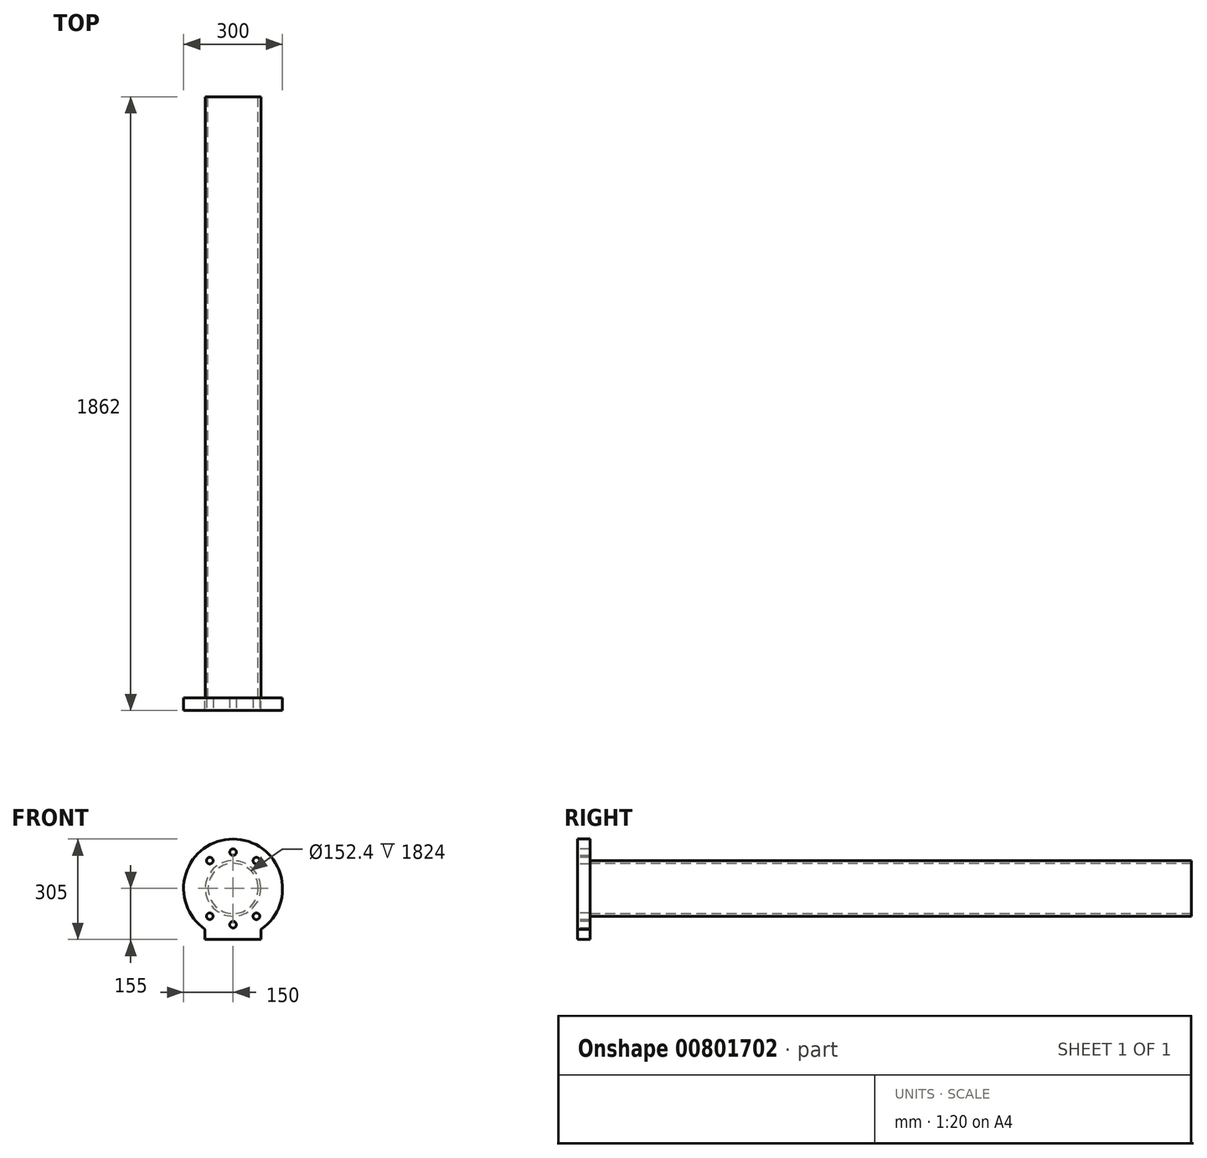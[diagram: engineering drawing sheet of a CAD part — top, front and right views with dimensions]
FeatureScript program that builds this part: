
annotation { "Feature Type Name" : "Feature", "Feature Type Description" : "" }
export const myFeature = defineFeature(function(context is Context, id is Id, definition is map)
    precondition{}
    {
        {
            var Q0;
            Q0=qCreatedBy(makeId("Front.planeOp"),FACE);
            var sketch = newSketch(context, id + "F0", { "sketchPlane" : qUnion([Q0])});
            skCircle(sketch, "E0", {"center": v(0, 0) * mm, "radius": 84.2 * mm});
            skCircle(sketch, "E1", {"center": v(0, 0) * mm, "radius": 76.2 * mm});
            skSolve(sketch);
        }
        {
            var Q0;
            Q0=makeQuery(id+"F0.imprint","IMPRINT",FACE,{"disambiguationData":[TD([[makeQuery(id+"F0.imprint","IMPRINT",EDGE,{"derivedFrom":sQuery(id+"F0.wireOp",EDGE,"E0")}),1.0]])]});
            extrude(context, id + "F1", {"entities" : qUnion([Q0]), "endBound" : BoundingType.SYMMETRIC, "depth" : 1824 * mm, "offsetDistance" : 25 * mm});
        }
        {
            var Q0;
            Q0=makeQuery(id+"F1.opExtrude","CAP_FACE",FACE,{"disambiguationData":[OSD([sQuery(id+"F0.wireOp",EDGE,"E0"),sQuery(id+"F0.wireOp",EDGE,"E1")])],"isStart":false});
            var sketch = newSketch(context, id + "F2", { "sketchPlane" : qUnion([Q0])});
            skCircle(sketch, "E2", {"center": v(0, 0) * mm, "radius": 75 * mm});
            skSolve(sketch);
        }
        {
            var Q0;
            Q0 = qSketchRegion(id + "F2", true);
            extrude(context, id + "F3", {"entities" : qUnion([Q0]), "operationType" : NewBodyOperationType.ADD, "depth" : 10 * mm, "offsetDistance" : 25 * mm});
        }
        {
            var Q0;
            Q0=makeQuery(id+"F3.opExtrude","CAP_FACE",FACE,{"disambiguationData":[OSD([sQuery(id+"F2.wireOp",EDGE,"E2")])],"isStart":false});
            var sketch = newSketch(context, id + "F4", { "sketchPlane" : qUnion([Q0])});
            skCircle(sketch, "E3", {"center": v(-52.83, 30.5) * mm, "radius": 10 * mm});
            skCircle(sketch, "E4", {"center": v(0, 0) * mm, "radius": 61 * mm, "construction": true});
            skLineSegment(sketch, "E5", {"start": v(0, 0) * mm, "end": v(0, 75) * mm, "construction": true});
            skLineSegment(sketch, "E6", {"start": v(0, 0) * mm, "end": v(-52.83, 30.5) * mm, "construction": true});
            skCircle(sketch, "E7.1.0", {"center": v(-52.83, -30.5) * mm, "radius": 10 * mm});
            skCircle(sketch, "E7.2.0", {"center": v(0, -61) * mm, "radius": 10 * mm});
            skCircle(sketch, "E8.1.3.0", {"center": v(52.83, -30.5) * mm, "radius": 10 * mm});
            skCircle(sketch, "E8.1.4.0", {"center": v(52.83, 30.5) * mm, "radius": 10 * mm});
            skCircle(sketch, "E8.1.5.0", {"center": v(0, 61) * mm, "radius": 10 * mm});
            skSolve(sketch);
        }
        {
            var Q0;
            Q0=makeQuery(id+"F4.imprint","IMPRINT",FACE,{"disambiguationData":[TD([[makeQuery(id+"F4.imprint","IMPRINT",EDGE,{"derivedFrom":sQuery(id+"F4.wireOp",EDGE,"E8.1.5.0")}),1.0]])]});
            var Q1;
            Q1=makeQuery(id+"F4.imprint","IMPRINT",FACE,{"disambiguationData":[TD([[makeQuery(id+"F4.imprint","IMPRINT",EDGE,{"derivedFrom":sQuery(id+"F4.wireOp",EDGE,"E3")}),1.0]])]});
            var Q2;
            Q2=makeQuery(id+"F4.imprint","IMPRINT",FACE,{"disambiguationData":[TD([[makeQuery(id+"F4.imprint","IMPRINT",EDGE,{"derivedFrom":sQuery(id+"F4.wireOp",EDGE,"E7.1.0")}),1.0]])]});
            var Q3;
            Q3=makeQuery(id+"F4.imprint","IMPRINT",FACE,{"disambiguationData":[TD([[makeQuery(id+"F4.imprint","IMPRINT",EDGE,{"derivedFrom":sQuery(id+"F4.wireOp",EDGE,"E7.2.0")}),1.0]])]});
            var Q4;
            Q4=makeQuery(id+"F4.imprint","IMPRINT",FACE,{"disambiguationData":[TD([[makeQuery(id+"F4.imprint","IMPRINT",EDGE,{"derivedFrom":sQuery(id+"F4.wireOp",EDGE,"E8.1.3.0")}),1.0]])]});
            var Q5;
            Q5=makeQuery(id+"F4.imprint","IMPRINT",FACE,{"disambiguationData":[TD([[makeQuery(id+"F4.imprint","IMPRINT",EDGE,{"derivedFrom":sQuery(id+"F4.wireOp",EDGE,"E8.1.4.0")}),1.0]])]});
            var Q6;
            {var subQ0=sQuery(id+"F2.wireOp",EDGE,"E2");Q6=makeQuery(id+"F3.boolean.opBoolean","SPLIT",FACE,{"disambiguationData":[TD([makeQuery(id+"F1.opExtrude","SWEPT_FACE",FACE,{"disambiguationData":[OSD([sQuery(id+"F0.wireOp",EDGE,"E0")])]})])],"derivedFrom":makeQuery(id+"F3.opExtrude","CAP_FACE",FACE,{"disambiguationData":[OSD([subQ0])],"isStart":true})});}
            extrude(context, id + "F5", {"entities" : qUnion([Q0, Q1, Q2, Q3, Q4, Q5]), "operationType" : NewBodyOperationType.REMOVE, "endBound" : BoundingType.UP_TO_SURFACE, "oppositeDirection" : true, "depth" : 25 * mm, "endBoundEntityFace" : qUnion([Q6]), "offsetDistance" : 25 * mm});
        }
        {
            var Q0;
            Q0=makeQuery(id+"FU2U09leFn4y694_1.1.F3.opExtrude","SWEPT_BODY",BODY,{"disambiguationData":[OSD([sQuery(id+"F2.wireOp",EDGE,"E2")])]});
            var Q1;
            Q1=makeQuery(id+"F3.opExtrude","SWEPT_BODY",BODY,{"disambiguationData":[OSD([sQuery(id+"F2.wireOp",EDGE,"E2")])]});
            deleteBodies(context, id + "F6", {"entities" : qUnion([Q0, Q1])});
        }
        {
            var Q0;
            Q0=makeQuery(id+"F1.opExtrude","CAP_FACE",FACE,{"disambiguationData":[OSD([sQuery(id+"F0.wireOp",EDGE,"E0"),sQuery(id+"F0.wireOp",EDGE,"E1")])],"isStart":false});
            var sketch = newSketch(context, id + "F7", { "sketchPlane" : qUnion([Q0])});
            skArc(sketch, "E9", {"start": v(85, -123.6) * mm, "mid": v(0, 150) * mm, "end": v(-85, -123.6) * mm});
            skLineSegment(sketch, "E10", {"start": v(-85, -155) * mm, "end": v(85, -155) * mm});
            skLineSegment(sketch, "E11", {"start": v(0, -150) * mm, "end": v(85, -150) * mm, "construction": true});
            skLineSegment(sketch, "E12", {"start": v(-85, -155) * mm, "end": v(-85, -123.6) * mm});
            skLineSegment(sketch, "E13", {"start": v(85, -155) * mm, "end": v(85, -123.6) * mm});
            skSolve(sketch);
        }
        {
            var Q0;
            Q0 = qSketchRegion(id + "F7", true);
            extrude(context, id + "F8", {"entities" : qUnion([Q0]), "operationType" : NewBodyOperationType.ADD, "depth" : 38 * mm, "offsetDistance" : 25 * mm});
        }
        {
            var Q0;
            Q0=makeQuery(id+"F8.opExtrude","CAP_FACE",FACE,{"disambiguationData":[OSD([sQuery(id+"F7.wireOp",EDGE,"E9"),sQuery(id+"F7.wireOp",EDGE,"E10"),sQuery(id+"F7.wireOp",EDGE,"E12"),sQuery(id+"F7.wireOp",EDGE,"E13")])],"isStart":false});
            var sketch = newSketch(context, id + "F9", { "sketchPlane" : qUnion([Q0])});
            skCircle(sketch, "E14", {"center": v(-70.7, 84.26) * mm, "radius": 10 * mm});
            skCircle(sketch, "E15", {"center": v(0, 110) * mm, "radius": 10 * mm});
            skCircle(sketch, "E16", {"center": v(70.7, 84.26) * mm, "radius": 10 * mm});
            skLineSegment(sketch, "E17", {"start": v(0, 0) * mm, "end": v(-150, 0) * mm, "construction": true});
            skLineSegment(sketch, "E18", {"start": v(0, 0) * mm, "end": v(0, 150) * mm, "construction": true});
            skCircle(sketch, "E19", {"center": v(0, 0) * mm, "radius": 110 * mm, "construction": true});
            skLineSegment(sketch, "E20", {"start": v(0, 0) * mm, "end": v(-70.7, 84.26) * mm, "construction": true});
            skLineSegment(sketch, "E21", {"start": v(0, 0) * mm, "end": v(70.7, 84.26) * mm, "construction": true});
            skCircle(sketch, "E22.MirrorC", {"center": v(-70.7, -84.26) * mm, "radius": 10 * mm});
            skCircle(sketch, "E23.MirrorC", {"center": v(0, -110) * mm, "radius": 10 * mm});
            skCircle(sketch, "E24.MirrorC", {"center": v(70.7, -84.26) * mm, "radius": 10 * mm});
            skSolve(sketch);
        }
        {
            var Q0;
            Q0 = qSketchRegion(id + "F9", true);
            var Q1;
            {var subQ0=sQuery(id+"F7.wireOp",EDGE,"E12");var subQ1=sQuery(id+"F7.wireOp",EDGE,"E9");var subQ2=sQuery(id+"F7.wireOp",EDGE,"E10");var subQ3=sQuery(id+"F7.wireOp",EDGE,"E13");Q1=makeQuery(id+"F8.boolean.opBoolean","SPLIT",FACE,{"disambiguationData":[TD([makeQuery(id+"F1.opExtrude","SWEPT_FACE",FACE,{"disambiguationData":[OSD([sQuery(id+"F0.wireOp",EDGE,"E0")])]})])],"derivedFrom":makeQuery(id+"F8.opExtrude","CAP_FACE",FACE,{"disambiguationData":[OSD([subQ1,subQ2,subQ0,subQ3])],"isStart":true})});}
            extrude(context, id + "F10", {"entities" : qUnion([Q0]), "operationType" : NewBodyOperationType.REMOVE, "endBound" : BoundingType.UP_TO_SURFACE, "oppositeDirection" : true, "depth" : 25 * mm, "endBoundEntityFace" : qUnion([Q1]), "offsetDistance" : 25 * mm});
        }
    });
